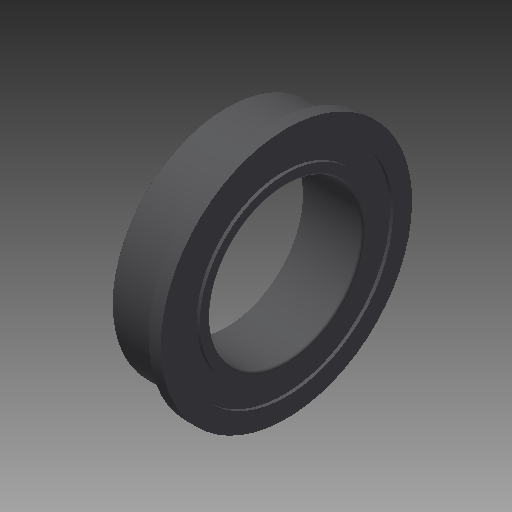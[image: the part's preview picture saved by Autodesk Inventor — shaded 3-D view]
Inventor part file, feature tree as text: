
AUTODESK INVENTOR PART (.ipt)
format: ipt  version: 2017 (Build 210142000, 142)  size: 186,368 bytes
history: native  units: mm
features: other x7, revolve x1, sketch x1
ambient origin geometry x8: Origin, YZ Plane, XZ Plane, XY Plane, X Axis, Y Axis, Z Axis, Center Point
bodies: Solid1 (feature_tree)
feature tree (9):
  revolve  "Revolution1"  [1 undecoded]
  other  "to_housing_XY"
  other  "to_housing_YZ"
  other  "to_housing_ZX"
  other  "to_housing_X"
  other  "to_housing_Y"
  other  "to_housing_Z"
  other  "to_housing_Center"
  sketch  "Sketch_1"  dims[d0=360.0deg d1=0.0mm]
note: 1 required parameter value undecoded (feature->parameter linkage not recoverable at this tier; creation-order binding heuristic only, values carry confidence <= 0.55)
